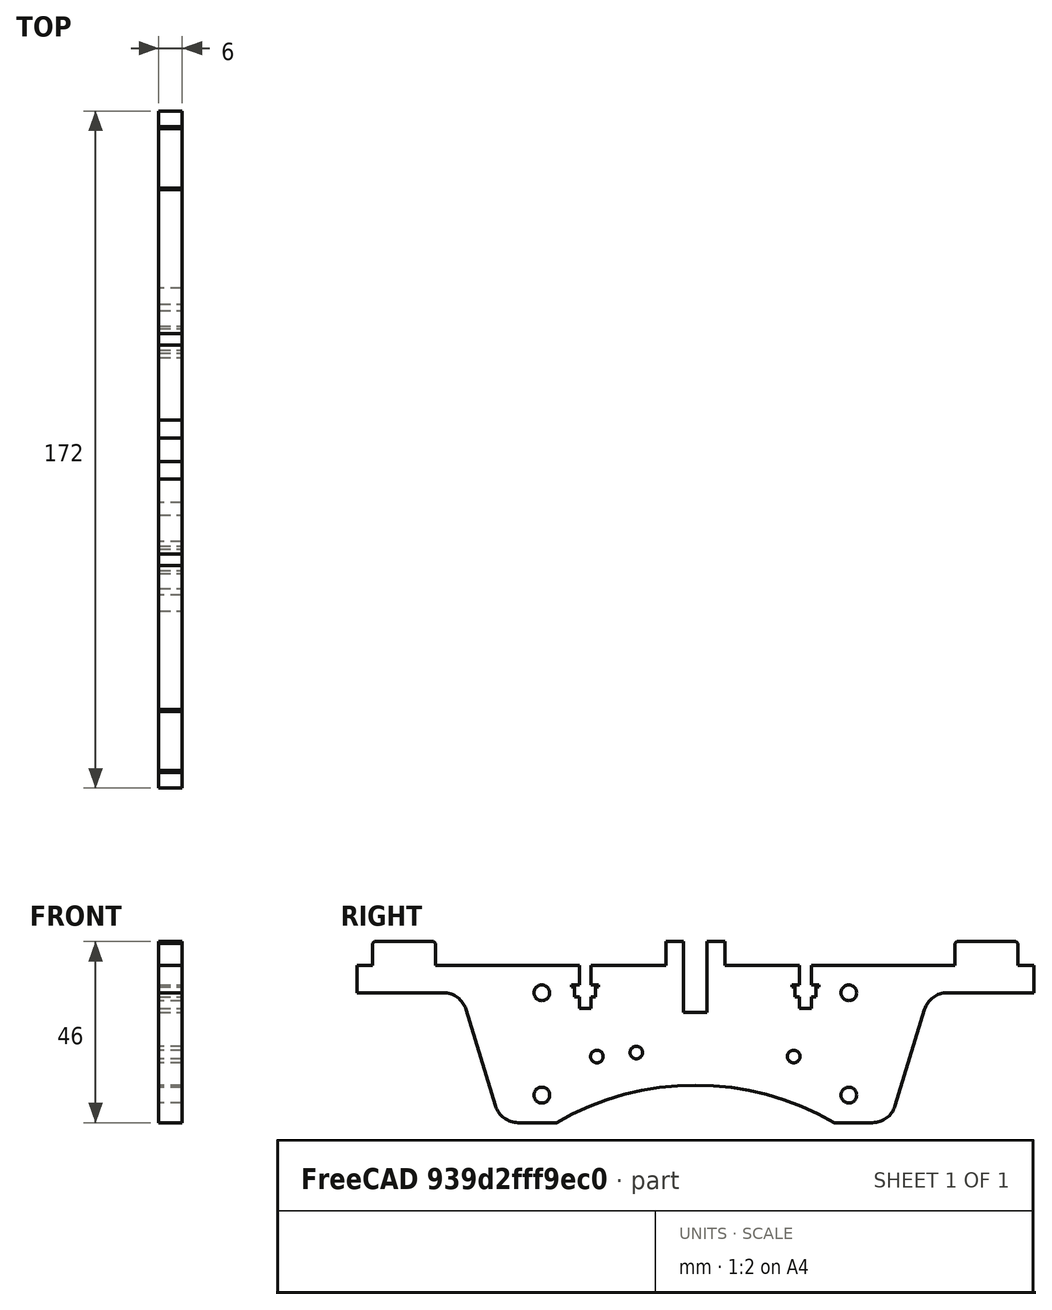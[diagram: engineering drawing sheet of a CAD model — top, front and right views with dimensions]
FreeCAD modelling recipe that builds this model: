
FCSTD DOCUMENT  (FreeCAD 0.17R13541 (Git))
Label: xx_xxx_y-rib
License: All rights reserved
LicenseURL: http://en.wikipedia.org/wiki/All_rights_reserved
objects: Sketcher::SketchObject×1, PartDesign::Pad×1, PartDesign::Body×1
note: 4 computed .brp shape members not serialized (recipe doc carries the construction recipe); baked Part::Feature solids carry a one-line shape summary decoded from their .brp

FEATURE [Sketcher::SketchObject] Sketch073
  MapMode = 5
  Placement = pos=(0,0,0) rot=(0.57735,0.57735,0.57735;2.0944rad)
  Support = -> [YZ_Plane]
  sketch-geometry (73):
    g0: Circle CenterX=-39 CenterY=13 CenterZ=0 NormalX=0 NormalY=0 NormalZ=-1 AngleXU=0 Radius=2
    g1: Circle CenterX=39 CenterY=13 CenterZ=0 NormalX=0 NormalY=0 NormalZ=-1 AngleXU=0 Radius=2
    g2: LineSegment StartX=26.52 StartY=20 StartZ=0 EndX=7.5 EndY=20 EndZ=0
    g3: Circle CenterX=-25 CenterY=-3.2 CenterZ=0 NormalX=0 NormalY=0 NormalZ=-1 AngleXU=0 Radius=1.6
    g4: LineSegment StartX=-66.5 StartY=26 StartZ=0 EndX=-81.5 EndY=26 EndZ=0
    g5: LineSegment StartX=-25.3 StartY=12 StartZ=0 EndX=-25.3 EndY=14.5 EndZ=0
    g6: LineSegment StartX=7.5 StartY=26 StartZ=0 EndX=3 EndY=26 EndZ=0
    g7: ArcOfCircle CenterX=64 CenterY=7 CenterZ=0 NormalX=0 NormalY=0 NormalZ=1 AngleXU=0 Radius=6 StartAngle=1.5708 EndAngle=2.84372
    g8: LineSegment StartX=50.7358 StartY=-15.7609 StartZ=0 EndX=58.2642 EndY=8.76094 EndZ=0
    g9: LineSegment StartX=7.5 StartY=20 StartZ=0 EndX=7.5 EndY=26 EndZ=0
    g10: Circle CenterX=-15 CenterY=-2.2 CenterZ=0 NormalX=0 NormalY=0 NormalZ=-1 AngleXU=0 Radius=1.6
    g11: Circle CenterX=39 CenterY=-13 CenterZ=0 NormalX=0 NormalY=0 NormalZ=-1 AngleXU=0 Radius=2
    g12: LineSegment StartX=-82 StartY=20 StartZ=0 EndX=-86 EndY=20 EndZ=0
    g13: LineSegment StartX=-31.45 StartY=15 StartZ=0 EndX=-31.45 EndY=14.5 EndZ=0
    g14: LineSegment StartX=86 StartY=20 StartZ=0 EndX=82 EndY=20 EndZ=0
    g15: LineSegment StartX=-45 StartY=-20 StartZ=0 EndX=-35.3214 EndY=-20 EndZ=0
    g16: LineSegment StartX=-81.5 StartY=26 StartZ=0 EndX=-82 EndY=25.5 EndZ=0
    g17: LineSegment StartX=66.5 StartY=26 StartZ=0 EndX=66 EndY=25.5 EndZ=0
    g18: LineSegment StartX=31.45 StartY=14.5 StartZ=0 EndX=31.45 EndY=15 EndZ=0
    g19: Circle CenterX=-39 CenterY=-13 CenterZ=0 NormalX=0 NormalY=0 NormalZ=-1 AngleXU=0 Radius=2
    g20: LineSegment StartX=-29.48 StartY=12 StartZ=0 EndX=-29.48 EndY=9 EndZ=0
    g21: LineSegment StartX=-29.48 StartY=9 StartZ=0 EndX=-26.52 EndY=9 EndZ=0
    g22: ArcOfCircle CenterX=-45 CenterY=-14 CenterZ=0 NormalX=0 NormalY=0 NormalZ=1 AngleXU=0 Radius=6 StartAngle=3.43947 EndAngle=4.71239
    g23: LineSegment StartX=30.7 StartY=12 StartZ=0 EndX=30.7 EndY=14.5 EndZ=0
    g24: LineSegment StartX=25.3 StartY=14.5 StartZ=0 EndX=25.3 EndY=12 EndZ=0
    g25: LineSegment StartX=-66 StartY=20 StartZ=0 EndX=-66 EndY=25.5 EndZ=0
    g26: LineSegment StartX=86 StartY=13 StartZ=0 EndX=86 EndY=20 EndZ=0
    g27: LineSegment StartX=29.48 StartY=9 StartZ=0 EndX=29.48 EndY=12 EndZ=0
    g28: LineSegment StartX=-29.48 StartY=20 StartZ=0 EndX=-29.48 EndY=15 EndZ=0
    g29: LineSegment StartX=24.55 StartY=15 StartZ=0 EndX=24.55 EndY=14.5 EndZ=0
    g30: LineSegment StartX=64 StartY=13 StartZ=0 EndX=86 EndY=13 EndZ=0
    g31: LineSegment StartX=35.3214 StartY=-20 StartZ=0 EndX=45 EndY=-20 EndZ=0
    g32: LineSegment StartX=3 StartY=26 StartZ=0 EndX=3 EndY=8 EndZ=0
    g33: LineSegment StartX=-82 StartY=25.5 StartZ=0 EndX=-82 EndY=20 EndZ=0
    g34: LineSegment StartX=-24.55 StartY=15 StartZ=0 EndX=-26.52 EndY=15 EndZ=0
    g35: LineSegment StartX=-86 StartY=20 StartZ=0 EndX=-86 EndY=13 EndZ=0
    g36: ArcOfCircle CenterX=45 CenterY=-14 CenterZ=0 NormalX=0 NormalY=0 NormalZ=1 AngleXU=0 Radius=6 StartAngle=4.71239 EndAngle=5.98531
    g37: LineSegment StartX=-30.7 StartY=14.5 StartZ=0 EndX=-30.7 EndY=12 EndZ=0
    g38: LineSegment StartX=-3 StartY=8 StartZ=0 EndX=-3 EndY=26 EndZ=0
    g39: LineSegment StartX=-31.45 StartY=14.5 StartZ=0 EndX=-30.7 EndY=14.5 EndZ=0
    g40: LineSegment StartX=-26.52 StartY=15 StartZ=0 EndX=-26.52 EndY=20 EndZ=0
    g41: LineSegment StartX=-3 StartY=26 StartZ=0 EndX=-7.5 EndY=26 EndZ=0
    g42: LineSegment StartX=29.48 StartY=12 StartZ=0 EndX=30.7 EndY=12 EndZ=0
    g43: LineSegment StartX=-58.2642 StartY=8.76094 StartZ=0 EndX=-50.7358 EndY=-15.7609 EndZ=0
    g44: LineSegment StartX=26.52 StartY=12 StartZ=0 EndX=26.52 EndY=9 EndZ=0
    g45: LineSegment StartX=-26.52 StartY=12 StartZ=0 EndX=-25.3 EndY=12 EndZ=0
    g46: LineSegment StartX=26.52 StartY=20 StartZ=0 EndX=26.52 EndY=15 EndZ=0
    g47: LineSegment StartX=30.7 StartY=14.5 StartZ=0 EndX=31.45 EndY=14.5 EndZ=0
    g48: LineSegment StartX=66 StartY=20 StartZ=0 EndX=29.48 EndY=20 EndZ=0
    g49: LineSegment StartX=81.5 StartY=26 StartZ=0 EndX=66.5 EndY=26 EndZ=0
    g50: LineSegment StartX=-7.5 StartY=26 StartZ=0 EndX=-7.5 EndY=20 EndZ=0
    g51: LineSegment StartX=-30.7 StartY=12 StartZ=0 EndX=-29.48 EndY=12 EndZ=0
    g52: LineSegment StartX=26.52 StartY=15 StartZ=0 EndX=24.55 EndY=15 EndZ=0
    g53: LineSegment StartX=25.3 StartY=12 StartZ=0 EndX=26.52 EndY=12 EndZ=0
    g54: LineSegment StartX=-29.48 StartY=20 StartZ=0 EndX=-66 EndY=20 EndZ=0
    g55: LineSegment StartX=82 StartY=20 StartZ=0 EndX=82 EndY=25.5 EndZ=0
    g56: LineSegment StartX=-24.55 StartY=14.5 StartZ=0 EndX=-24.55 EndY=15 EndZ=0
    g57: Circle CenterX=25 CenterY=-3.2 CenterZ=0 NormalX=0 NormalY=0 NormalZ=-1 AngleXU=0 Radius=1.6
    g58: LineSegment StartX=-26.52 StartY=9 StartZ=0 EndX=-26.52 EndY=12 EndZ=0
    g59: LineSegment StartX=-66 StartY=25.5 StartZ=0 EndX=-66.5 EndY=26 EndZ=0
    g60: ArcOfCircle CenterX=0 CenterY=-80.9132 CenterZ=0 NormalX=0 NormalY=0 NormalZ=1 AngleXU=0 Radius=70.4132 StartAngle=1.04531 EndAngle=2.09628
    g61: LineSegment StartX=-86 StartY=13 StartZ=0 EndX=-64 EndY=13 EndZ=0
    g62: LineSegment StartX=26.52 StartY=9 StartZ=0 EndX=29.48 EndY=9 EndZ=0
    g63: LineSegment StartX=24.55 StartY=14.5 StartZ=0 EndX=25.3 EndY=14.5 EndZ=0
    g64: LineSegment StartX=-7.5 StartY=20 StartZ=0 EndX=-26.52 EndY=20 EndZ=0
    g65: LineSegment StartX=82 StartY=25.5 StartZ=0 EndX=81.5 EndY=26 EndZ=0
    g66: LineSegment StartX=66 StartY=25.5 StartZ=0 EndX=66 EndY=20 EndZ=0
    g67: ArcOfCircle CenterX=-64 CenterY=7 CenterZ=0 NormalX=0 NormalY=0 NormalZ=1 AngleXU=0 Radius=6 StartAngle=0.297875 EndAngle=1.5708
    g68: LineSegment StartX=31.45 StartY=15 StartZ=0 EndX=29.48 EndY=15 EndZ=0
    g69: LineSegment StartX=-29.48 StartY=15 StartZ=0 EndX=-31.45 EndY=15 EndZ=0
    g70: LineSegment StartX=-25.3 StartY=14.5 StartZ=0 EndX=-24.55 EndY=14.5 EndZ=0
    g71: LineSegment StartX=29.48 StartY=15 StartZ=0 EndX=29.48 EndY=20 EndZ=0
    g72: LineSegment StartX=3 StartY=8 StartZ=0 EndX=-3 EndY=8 EndZ=0
  constraints (66):
    c: Coincident(g35,g61)
    c: Coincident(g12,g35)
    c: Coincident(g33,g12)
    c: Coincident(g33,g16)
    c: Coincident(g4,g16)
    c: Coincident(g4,g59)
    c: Coincident(g54,g25)
    c: Coincident(g59,g25)
    c: Coincident(g61,g67)
    c: Coincident(g43,g67)
    c: Coincident(g43,g22)
    c: Coincident(g15,g22)
    c: Coincident(g60,g15)
    c: Coincident(g39,g13)
    c: Coincident(g13,g69)
    c: Coincident(g51,g37)
    c: Coincident(g39,g37)
    c: Coincident(g21,g20)
    c: Coincident(g20,g51)
    c: Coincident(g28,g69)
    c: Coincident(g54,g28)
    c: Coincident(g21,g58)
    c: Coincident(g58,g45)
    c: Coincident(g34,g40)
    c: Coincident(g64,g40)
    c: Coincident(g5,g45)
    c: Coincident(g70,g5)
    c: Coincident(g56,g70)
    c: Coincident(g56,g34)
    c: Coincident(g64,g50)
    c: Coincident(g41,g50)
    c: Coincident(g38,g72)
    c: Coincident(g38,g41)
    c: Coincident(g72,g32)
    c: Coincident(g32,g6)
    c: Coincident(g2,g9)
    c: Coincident(g6,g9)
    c: Coincident(g63,g29)
    c: Coincident(g52,g29)
    c: Coincident(g24,g53)
    c: Coincident(g63,g24)
    c: Coincident(g62,g44)
    c: Coincident(g44,g53)
    c: Coincident(g46,g52)
    c: Coincident(g2,g46)
    c: Coincident(g27,g62)
    c: Coincident(g42,g27)
    c: Coincident(g71,g68)
    c: Coincident(g71,g48)
    c: Coincident(g42,g23)
    c: Coincident(g47,g23)
    c: Coincident(g47,g18)
    c: Coincident(g18,g68)
    c: Coincident(g60,g31)
    c: Coincident(g31,g36)
    c: Coincident(g8,g36)
    c: Coincident(g7,g8)
    c: Coincident(g30,g7)
    c: Coincident(g66,g48)
    c: Coincident(g66,g17)
    c: Coincident(g17,g49)
    c: Coincident(g65,g49)
    c: Coincident(g14,g55)
    c: Coincident(g65,g55)
    c: Coincident(g26,g30)
    c: Coincident(g14,g26)
FEATURE [PartDesign::Pad] Pad
  Length = 6
  Length2 = 100
  Placement = pos=(0,0,0) rot=(0.57735,0.57735,0.57735;2.0944rad)
  Profile = -> Sketch073
  Type = 0
FEATURE [PartDesign::Body] Body
  Group = -> [Sketch073,Pad]
  Origin = -> Origin
  Tip = -> Pad
